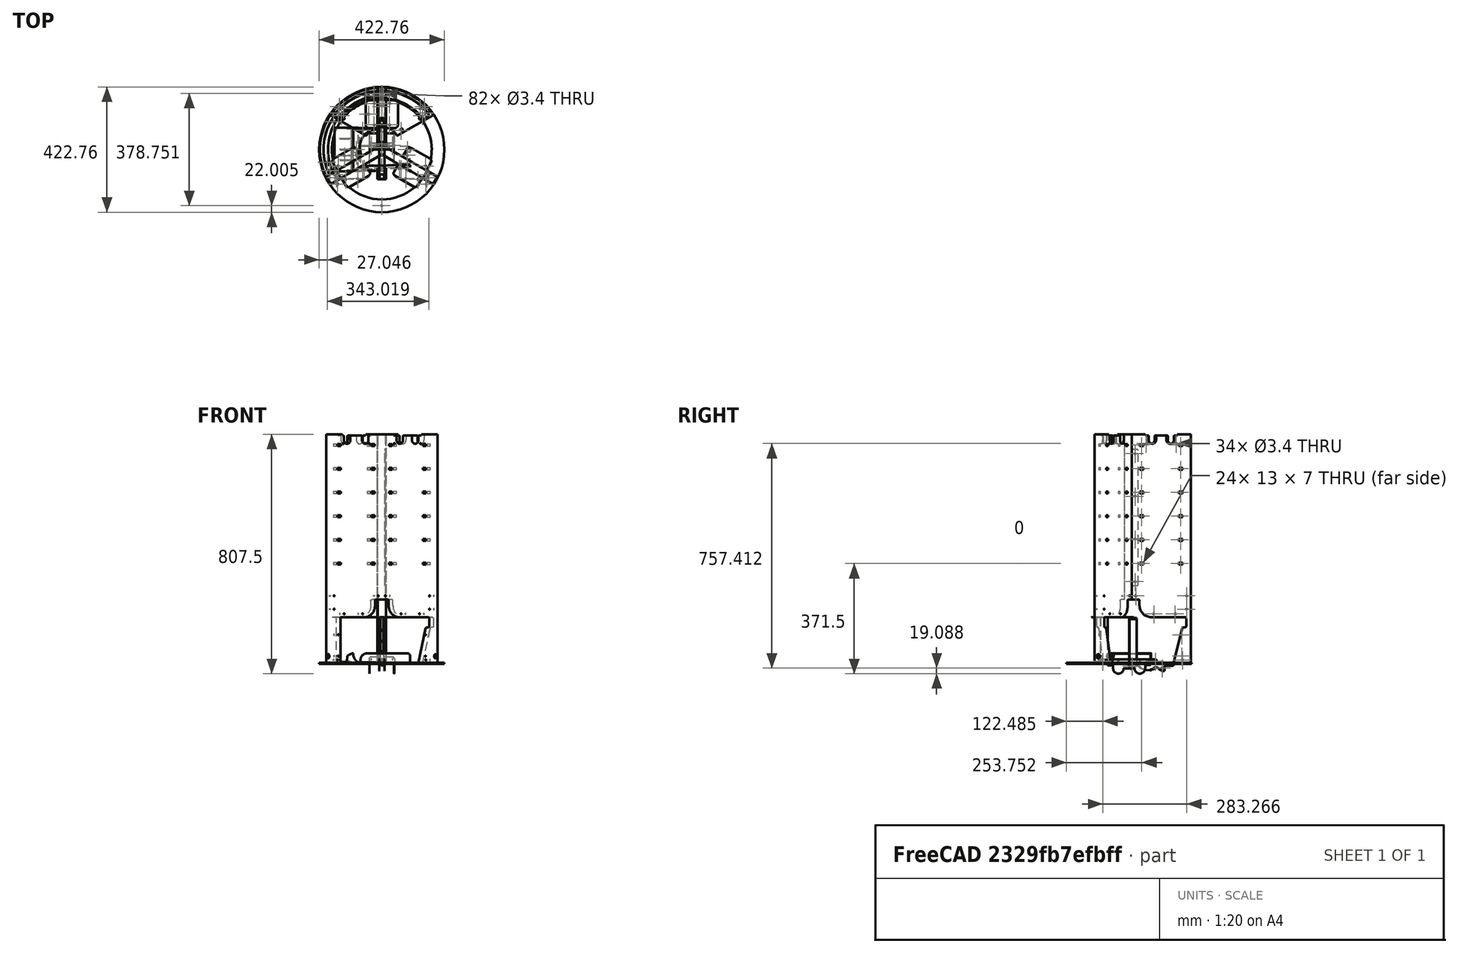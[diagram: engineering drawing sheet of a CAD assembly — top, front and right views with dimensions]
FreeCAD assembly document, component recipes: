
FREECAD ASSEMBLY — COMPONENT RECIPES ("composit_stand2_reserve")

This assembly document has 21 components, labeled P0..P20 below (a component is one placed body or linked part). 21 of them carry a construction recipe — the FreeCAD feature program that regenerates the part from scratch, quoted from this document or its linked companion documents; the rest are supplied as boundary geometry only. No exploded tour is included for this assembly.
NOTE — document 2 of 2 of this assembly tour. The two overview renders and the header above are repeated from document 1; the component sections below continue where the previous document stopped.
COMPONENT P18 — recipe-attached ("gutter_bottom_material_0.30ansi", modeled in this document).
Construction recipe (the document's own serialized feature program — sketch geometry with constraints, then the solid features built on it; lengths are millimeters unless a unit is written):

FEATURE [Sketcher::SketchObject] Sketch134
  FullyConstrained = true
  MapMode = 5
  Placement = pos=(0,0,0) rot=(1,0,0;1.5708rad)
  Support = -> [XZ_Plane044]
  sketch-geometry (5):
    g0: LineSegment StartX=-8.5 StartY=15 StartZ=0 EndX=-8.5 EndY=0 EndZ=0
    g1: LineSegment StartX=-8.5 StartY=0 StartZ=0 EndX=8.5 EndY=0 EndZ=0
    g2: LineSegment StartX=8.5 StartY=0 StartZ=0 EndX=8.5 EndY=15 EndZ=0
    g3: LineSegment StartX=8.5 StartY=15 StartZ=0 EndX=-8.5 EndY=15 EndZ=0
    g4: GeomPoint X=0 Y=7.5 Z=0
  constraints (13):
    c: Coincident(g0,g1)
    c: Coincident(g1,g2)
    c: Coincident(g2,g3)
    c: Coincident(g3,g0)
    c: Horizontal(g1)
    c: Horizontal(g3)
    c: Vertical(g0)
    c: Vertical(g2)
    c: Symmetric(g1,g0,g4)
    c: PointOnObject(g4,g-2)
    c: PointOnObject(g1,g-1)
    c: DistanceX(g1,g1) = 17  'width'
    c: DistanceY(g2) = 15  'height'
FEATURE [Sketcher::SketchObject] Sketch135
  FullyConstrained = true
  MapMode = 5
  Placement = pos=(0,0,0) rot=(1,0,0;1.5708rad)
  Support = -> [XZ_Plane044]
  sketch-geometry (1):
    g0: GeomPoint X=172 Y=45 Z=0
  constraints (3):
    c: DistanceX(g0) = 172
    c: DistanceY(g0) = 45
    c: Distance(g-1,g0) = 177.789  'length'
FEATURE [PartDesign::FeaturePython] BaseBend010  # WARN: FeaturePython — macro-defined, semantics opaque (R4)
  BendSide = 0
  BendSketch = -> Sketch134
  MidPlane = true
  Reverse = false
  length = 187.789
  radius = 0.1
  thickness = 0.3
FEATURE [Sketcher::SketchObject] Sketch136
  AttachmentOffset = pos=(0,8,0) rot=(0,0,1;0rad)
  FullyConstrained = true
  MapMode = 5
  Placement = pos=(-1.8e-15,1.8e-15,8) rot=(0.57735,0.57735,0.57735;2.0944rad)
  Support = -> [YZ_Plane044]
  sketch-geometry (2):
    g0: Circle CenterX=-88.8946 CenterY=0 CenterZ=0 NormalX=0 NormalY=0 NormalZ=1 AngleXU=0 Radius=1.7
    g1: Circle CenterX=88.8946 CenterY=0 CenterZ=0 NormalX=0 NormalY=0 NormalZ=1 AngleXU=0 Radius=1.7
  constraints (5):
    c: PointOnObject(g0,g-1)
    c: Symmetric(g0,g1,g-2)
    c: DistanceX(g0,g1) = 177.789
    c: Equal(g1,g0)
    c: Diameter(g1) = 3.4
FEATURE [Sketcher::SketchObject] Sketch137
  AttachmentOffset = pos=(93.8946,15,0) rot=(0,0,1;0rad)
  FullyConstrained = true
  MapMode = 5
  Placement = pos=(1.75e-14,93.8946,15) rot=(0.57735,0.57735,0.57735;2.0944rad)
  Support = -> [YZ_Plane044]
  sketch-geometry (3):
    g0: ArcOfCircle CenterX=-7 CenterY=-7 CenterZ=0 NormalX=0 NormalY=0 NormalZ=1 AngleXU=0 Radius=7 StartAngle=-3.2e-14 EndAngle=1.5708
    g1: LineSegment StartX=-7 StartY=0 StartZ=0 EndX=0 EndY=0 EndZ=0
    g2: LineSegment StartX=0 StartY=0 StartZ=0 EndX=0 EndY=-7 EndZ=0
  constraints (8):
    c: PointOnObject(g0,g-2)
    c: PointOnObject(g0,g-1)
    c: Coincident(g1,g2)
    c: Vertical(g2)
    c: Tangent(g2,g0) = 1.5708
    c: Tangent(g0,g1) = 1.5708
    c: DistanceY(g2,g2) = 7
    c: Horizontal(g1)
FEATURE [PartDesign::Pocket] Pocket092
  BaseFeature = -> BaseBend010
  Direction = (-1,2e-16,-3e-16)
  Length = 5
  Length2 = 5
  Midplane = true
  Profile = -> Sketch137
  ReferenceAxis = -> Sketch137 [N_Axis]
  Type = 1
FEATURE [PartDesign::Mirrored] Mirrored041
  BaseFeature = -> Pocket092
  MirrorPlane = -> XZ_Plane044
  Originals = -> [Pocket092]
FEATURE [Sketcher::SketchObject] Sketch138
  AttachmentOffset = pos=(0,-63.8946,0) rot=(0,0,1;0rad)
  FullyConstrained = false
  MapMode = 5
  Placement = pos=(0,-63.8946,0) rot=(0,0,1;0rad)
  Support = -> [XY_Plane045]
  sketch-geometry (5):
    g0: LineSegment StartX=-8.25 StartY=-159.942 StartZ=0 EndX=-8.25 EndY=0 EndZ=0
    g1: LineSegment StartX=-8.25 StartY=0 StartZ=0 EndX=8.25 EndY=0 EndZ=0
    g2: LineSegment StartX=8.25 StartY=0 StartZ=0 EndX=8.25 EndY=-159.942 EndZ=0
    g3: LineSegment StartX=8.25 StartY=-159.942 StartZ=0 EndX=-8.25 EndY=-159.942 EndZ=0
    g4: GeomPoint X=0 Y=-79.9711 Z=0
  constraints (12):
    c: Coincident(g0,g1)
    c: Coincident(g1,g2)
    c: Coincident(g2,g3)
    c: Coincident(g3,g0)
    c: Horizontal(g1)
    c: Horizontal(g3)
    c: Vertical(g0)
    c: Vertical(g2)
    c: Symmetric(g1,g0,g4)
    c: PointOnObject(g4,g-2)
    c: PointOnObject(g1,g-1)
    c: DistanceX(g1,g1) = 16.5
FEATURE [PartDesign::Pocket] Pocket093
  BaseFeature = -> Mirrored041
  Direction = (0,0,-1)
  Length = 5
  Length2 = 5
  Profile = -> Sketch138
  ReferenceAxis = -> Sketch138 [N_Axis]
  Type = 1
FEATURE [Sketcher::SketchObject] Sketch139
  AttachmentOffset = pos=(-93.8946,0,0) rot=(0,0,1;0rad)
  FullyConstrained = true
  MapMode = 5
  Placement = pos=(-2.08e-14,-93.8946,2.08e-14) rot=(0.57735,0.57735,0.57735;2.0944rad)
  Support = -> [YZ_Plane044]
  sketch-geometry (4):
    g0: ArcOfCircle CenterX=5 CenterY=5.1 CenterZ=0 NormalX=0 NormalY=0 NormalZ=1 AngleXU=0 Radius=5 StartAngle=3.14159 EndAngle=4.71239
    g1: LineSegment StartX=0 StartY=5.1 StartZ=0 EndX=0 EndY=-0.3 EndZ=0
    g2: LineSegment StartX=0 StartY=-0.3 StartZ=0 EndX=5 EndY=-0.3 EndZ=0
    g3: LineSegment StartX=5 StartY=-0.3 StartZ=0 EndX=5 EndY=0.1 EndZ=0
  constraints (12):
    c: PointOnObject(g0,g-2)
    c: PointOnObject(g1,g-2)
    c: Coincident(g2,g1)
    c: Horizontal(g2)
    c: Coincident(g3,g2)
    c: Coincident(g3,g0)
    c: Vertical(g3)
    c: Perpendicular(g0,g3)
    c: Tangent(g1,g0) = -1.5708
    c: DistanceY(g0) = 0.1
    c: Diameter(g0) = 10
    c: DistanceY(g1) = -0.3
FEATURE [PartDesign::Pocket] Pocket094
  BaseFeature = -> Pocket093
  Direction = (-1,2e-16,-3e-16)
  Length = 5
  Length2 = 5
  Midplane = true
  Profile = -> Sketch139
  ReferenceAxis = -> Sketch139 [N_Axis]
  Type = 1
FEATURE [Sketcher::SketchObject] Sketch140
  FullyConstrained = true
  MapMode = 5
  Placement = pos=(0,0,0) rot=(0.57735,0.57735,0.57735;2.0944rad)
  Support = -> [YZ_Plane044]
  sketch-geometry (4):
    g0: LineSegment StartX=-163.895 StartY=-10 StartZ=0 EndX=-63.8946 EndY=-10 EndZ=0
    g1: LineSegment StartX=-63.8946 StartY=-10 StartZ=0 EndX=-63.8946 EndY=0.11 EndZ=0
    g2: LineSegment StartX=-63.8946 StartY=0.11 StartZ=0 EndX=-163.895 EndY=0.11 EndZ=0
    g3: LineSegment StartX=-163.895 StartY=0.11 StartZ=0 EndX=-163.895 EndY=-10 EndZ=0
  constraints (12):
    c: Coincident(g0,g1)
    c: Coincident(g1,g2)
    c: Coincident(g2,g3)
    c: Coincident(g3,g0)
    c: Horizontal(g0)
    c: Horizontal(g2)
    c: Vertical(g1)
    c: Vertical(g3)
    c: DistanceY(g2) = 0.11
    c: DistanceX(g1) = -63.8946
    c: DistanceY(g0) = -10
    c: DistanceX(g2,g2) = 100
FEATURE [PartDesign::Pocket] Pocket095
  BaseFeature = -> Pocket094
  Direction = (-1,2e-16,-3e-16)
  Length = 5
  Length2 = 5
  Midplane = true
  Profile = -> Sketch140
  ReferenceAxis = -> Sketch140 [N_Axis]
  Type = 1
FEATURE [PartDesign::Pocket] Pocket091
  BaseFeature = -> Pocket095
  Direction = (-1,2e-16,-3e-16)
  Length = 5
  Length2 = 5
  Midplane = true
  Profile = -> Sketch136
  ReferenceAxis = -> Sketch136 [N_Axis]
  Type = 1
FEATURE [PartDesign::Body] gutter_bottom  label="gutter_bottom_material_0.30ansi"
  Group = -> [Sketch134,Sketch135,BaseBend010,Sketch136,Sketch137,Pocket092,Mirrored041,Sketch138,Pocket093,Sketch139,Pocket094,Sketch140,Pocket095,Pocket091]
  Origin = -> Origin044
  Tip = -> Pocket091
COMPONENT P19 — recipe-attached ("tech_mid_material_0.50ansi", modeled in this document).
Construction recipe (the document's own serialized feature program — sketch geometry with constraints, then the solid features built on it; lengths are millimeters unless a unit is written):

FEATURE [PartDesign::CoordinateSystem] LCS_0007
  AttacherType = Attacher::AttachEngine3D
  MapMode = 2
  Support = -> [X_Axis038]
FEATURE [Sketcher::SketchObject] Sketch122
  FullyConstrained = true
  MapMode = 5
  Placement = pos=(0,0,0) rot=(0.57735,0.57735,0.57735;2.0944rad)
  Support = -> [YZ_Plane038]
  sketch-geometry (4):
    g0: LineSegment StartX=0 StartY=0 StartZ=0 EndX=15 EndY=0 EndZ=0
    g1: LineSegment StartX=15 StartY=0 StartZ=0 EndX=15 EndY=151 EndZ=0
    g2: LineSegment StartX=15 StartY=151 StartZ=0 EndX=0 EndY=151 EndZ=0
    g3: LineSegment StartX=0 StartY=151 StartZ=0 EndX=0 EndY=0 EndZ=0
  constraints (11):
    c: Coincident(g0,g1)
    c: Coincident(g1,g2)
    c: Coincident(g2,g3)
    c: Coincident(g3,g0)
    c: Horizontal(g0)
    c: Horizontal(g2)
    c: Vertical(g1)
    c: Vertical(g3)
    c: Coincident(g0,g-1)
    c: DistanceY(g2) = 151  'height'
    c: DistanceX(g0,g0) = 15  'length'
FEATURE [PartDesign::FeaturePython] BaseBend009  # WARN: FeaturePython — macro-defined, semantics opaque (R4)
  BendSide = 1
  BendSketch = -> Sketch122
  MidPlane = true
  Reverse = false
  length = 10
  radius = 0.1
  thickness = 0.3
FEATURE [Sketcher::SketchObject] Sketch123
  FullyConstrained = true
  MapMode = 5
  Support = -> [XY_Plane039]
  sketch-geometry (3):
    g0: Circle CenterX=0 CenterY=7.5 CenterZ=0 NormalX=0 NormalY=0 NormalZ=1 AngleXU=0 Radius=1.7
    g1: LineSegment StartX=0 StartY=0 StartZ=0 EndX=0 EndY=7.5 EndZ=0
    g2: LineSegment StartX=0 StartY=7.5 StartZ=0 EndX=0 EndY=15 EndZ=0
  constraints (8):
    c: PointOnObject(g0,g-2)
    c: Diameter(g0) = 3.4
    c: Coincident(g1,g-1)
    c: Coincident(g1,g0)
    c: Coincident(g2,g0)
    c: PointOnObject(g2,g-2)
    c: Equal(g2,g1)
    c: DistanceY(g2) = 15
FEATURE [PartDesign::Pocket] Pocket076
  BaseFeature = -> BaseBend009
  Direction = (0,0,-1)
  Length = 5
  Length2 = 5
  Midplane = true
  Profile = -> Sketch123
  ReferenceAxis = -> Sketch123 [N_Axis]
  Type = 1
FEATURE [Sketcher::SketchObject] Sketch124
  FullyConstrained = true
  MapMode = 5
  Placement = pos=(0,0,0) rot=(1,0,0;1.5708rad)
  Support = -> [XZ_Plane038]
  sketch-geometry (2):
    g0: Circle CenterX=0 CenterY=75.5 CenterZ=0 NormalX=0 NormalY=0 NormalZ=1 AngleXU=0 Radius=1.7
    g1: GeomPoint X=0 Y=151 Z=0
  constraints (4):
    c: PointOnObject(g0,g-2)
    c: DistanceY(g1) = 151
    c: Symmetric(g1,g-1,g0)
    c: Diameter(g0) = 3.4
FEATURE [PartDesign::Pocket] Pocket077
  BaseFeature = -> Pocket076
  Direction = (0,1,2e-16)
  Length = 5
  Length2 = 5
  Midplane = true
  Profile = -> Sketch124
  ReferenceAxis = -> Sketch124 [N_Axis]
  Type = 1
FEATURE [PartDesign::Body] tech_mid  label="tech_mid_material_0.50ansi"
  Group = -> [LCS_0007,Sketch122,BaseBend009,Sketch123,Pocket076,Sketch124,Pocket077]
  Origin = -> Origin038
  Tip = -> Pocket077
COMPONENT P20 — recipe-attached ("tech_pillar_material_0.50ansi", modeled in this document).
Construction recipe (the document's own serialized feature program — sketch geometry with constraints, then the solid features built on it; lengths are millimeters unless a unit is written):

FEATURE [PartDesign::CoordinateSystem] LCS_0006
  AttacherType = Attacher::AttachEngine3D
  MapMode = 2
  Support = -> [X_Axis037]
FEATURE [Sketcher::SketchObject] Sketch116
  FullyConstrained = true
  MapMode = 5
  Placement = pos=(0,0,0) rot=(0.57735,0.57735,0.57735;2.0944rad)
  Support = -> [YZ_Plane037]
  sketch-geometry (4):
    g0: LineSegment StartX=0 StartY=0 StartZ=0 EndX=25 EndY=0 EndZ=0
    g1: LineSegment StartX=25 StartY=0 StartZ=0 EndX=25 EndY=154 EndZ=0
    g2: LineSegment StartX=25 StartY=154 StartZ=0 EndX=0 EndY=154 EndZ=0
    g3: LineSegment StartX=0 StartY=154 StartZ=0 EndX=0 EndY=0 EndZ=0
  constraints (11):
    c: Coincident(g0,g1)
    c: Coincident(g1,g2)
    c: Coincident(g2,g3)
    c: Coincident(g3,g0)
    c: Horizontal(g0)
    c: Horizontal(g2)
    c: Vertical(g1)
    c: Vertical(g3)
    c: Coincident(g0,g-1)
    c: Distance(g3) = 154  'height'
    c: DistanceX(g0) = 25  'length'
FEATURE [PartDesign::FeaturePython] BaseBend008  # WARN: FeaturePython — macro-defined, semantics opaque (R4)
  BendSide = 1
  BendSketch = -> Sketch116
  MidPlane = true
  Reverse = false
  length = 25
  radius = 0.01
  thickness = 0.3
FEATURE [PartDesign::FeaturePython] Bend015  # WARN: FeaturePython — macro-defined, semantics opaque (R4)
  AutoMiter = true
  BaseFeature = -> BaseBend008
  BendType = 0
  LengthList = [25]
  LengthSpec = 1
  ReliefFactor = 0.7
  UseReliefFactor = false
  angle = 90
  baseObject = -> BaseBend008 [Edge26]
  bendAList = [90]
  extend1 = 0
  extend2 = 0
  gap1 = 3
  gap2 = 3
  invert = false
  kfactor = 0.5
  length = 25
  maxExtendDist = 5
  minGap = 0.1
  minReliefGap = 1
  miterangle1 = 0
  miterangle2 = 0
  offset = 0
  radius = 0.01
  reliefType = 0
  reliefd = 0.1
  reliefw = 0.1
  sketchflip = false
  sketchinvert = false
  unfold = false
FEATURE [PartDesign::FeaturePython] Bend016  # WARN: FeaturePython — macro-defined, semantics opaque (R4)
  AutoMiter = true
  BaseFeature = -> Bend015
  BendType = 0
  LengthList = [25]
  LengthSpec = 0
  ReliefFactor = 0.7
  UseReliefFactor = false
  angle = 90
  baseObject = -> Bend015 [Edge3]
  bendAList = [90]
  extend1 = 0
  extend2 = 0
  gap1 = 3
  gap2 = 0
  invert = false
  kfactor = 0.5
  length = 25
  maxExtendDist = 5
  minGap = 0.1
  minReliefGap = 1
  miterangle1 = 0
  miterangle2 = 0
  offset = 0
  radius = 0.01
  reliefType = 0
  reliefd = 0.1
  reliefw = 0.1
  sketchflip = false
  sketchinvert = false
  unfold = false
FEATURE [PartDesign::FeaturePython] Bend017  # WARN: FeaturePython — macro-defined, semantics opaque (R4)
  AutoMiter = true
  BaseFeature = -> Bend016
  BendType = 0
  LengthList = [25]
  LengthSpec = 0
  ReliefFactor = 0.7
  UseReliefFactor = false
  angle = 90
  baseObject = -> Bend016 [Edge24]
  bendAList = [90]
  extend1 = 0
  extend2 = 0
  gap1 = 0
  gap2 = 3
  invert = false
  kfactor = 0.5
  length = 25
  maxExtendDist = 5
  minGap = 0.1
  minReliefGap = 1
  miterangle1 = 0
  miterangle2 = 0
  offset = 0
  radius = 0.01
  reliefType = 0
  reliefd = 0.1
  reliefw = 0.1
  sketchflip = false
  sketchinvert = false
  unfold = false
FEATURE [Sketcher::SketchObject] Sketch117
  FullyConstrained = true
  MapMode = 5
  Support = -> [XY_Plane038]
  sketch-geometry (5):
    g0: Circle CenterX=0 CenterY=6 CenterZ=0 NormalX=0 NormalY=0 NormalZ=1 AngleXU=0 Radius=1.7
    g1: Circle CenterX=0 CenterY=19 CenterZ=0 NormalX=0 NormalY=0 NormalZ=1 AngleXU=0 Radius=1.7
    g2: LineSegment StartX=0 StartY=0 StartZ=0 EndX=0 EndY=6 EndZ=0
    g3: LineSegment StartX=0 StartY=6 StartZ=0 EndX=0 EndY=19 EndZ=0
    g4: LineSegment StartX=0 StartY=19 StartZ=0 EndX=0 EndY=25 EndZ=0
  constraints (13):
    c: PointOnObject(g0,g-2)
    c: PointOnObject(g1,g-2)
    c: Coincident(g2,g-1)
    c: Coincident(g2,g0)
    c: Coincident(g3,g0)
    c: Coincident(g3,g1)
    c: Coincident(g4,g1)
    c: PointOnObject(g4,g-2)
    c: DistanceY(g4) = 25
    c: Equal(g2,g4)
    c: Distance(g2) = 6
    c: Equal(g0,g1)
    c: Diameter(g0) = 3.4
FEATURE [PartDesign::Pocket] Pocket071
  BaseFeature = -> Bend017
  Direction = (0,0,-1)
  Length = 5
  Length2 = 5
  Midplane = true
  Profile = -> Sketch117
  ReferenceAxis = -> Sketch117 [N_Axis]
  Type = 1
FEATURE [Sketcher::SketchObject] Sketch118
  FullyConstrained = true
  MapMode = 5
  Placement = pos=(0,0,0) rot=(0.57735,0.57735,0.57735;2.0944rad)
  Support = -> [YZ_Plane037]
  sketch-geometry (4):
    g0: LineSegment StartX=60 StartY=130 StartZ=0 EndX=160 EndY=130 EndZ=0
    g1: LineSegment StartX=160 StartY=130 StartZ=0 EndX=160 EndY=180 EndZ=0
    g2: LineSegment StartX=160 StartY=180 StartZ=0 EndX=60 EndY=180 EndZ=0
    g3: LineSegment StartX=60 StartY=180 StartZ=0 EndX=60 EndY=130 EndZ=0
  constraints (12):
    c: Coincident(g0,g1)
    c: Coincident(g1,g2)
    c: Coincident(g2,g3)
    c: Coincident(g3,g0)
    c: Horizontal(g0)
    c: Horizontal(g2)
    c: Vertical(g1)
    c: Vertical(g3)
    c: DistanceY(g3,g3) = 50  'height'
    c: DistanceX(g0,g0) = 100  'length'
    c: DistanceX(g0) = 60
    c: DistanceY(g0) = 130
FEATURE [Sketcher::SketchObject] Sketch126
  FullyConstrained = true
  MapMode = 5
  Support = -> [XY_Plane038]
  sketch-geometry (3):
    g0: LineSegment StartX=12.5 StartY=25 StartZ=0 EndX=12.5 EndY=17.5 EndZ=0
    g1: LineSegment StartX=12.5 StartY=25 StartZ=0 EndX=5 EndY=25 EndZ=0
    g2: ArcOfCircle CenterX=5 CenterY=17.5 CenterZ=0 NormalX=0 NormalY=0 NormalZ=1 AngleXU=0 Radius=7.5 StartAngle=0 EndAngle=1.5708
  constraints (8):
    c: Vertical(g0)
    c: DistanceX(g0) = 12.5
    c: DistanceY(g0) = 25
    c: Coincident(g1,g0)
    c: Horizontal(g1)
    c: Tangent(g2,g0) = 1.5708
    c: Tangent(g2,g1) = -1.5708
    c: Diameter(g2) = 15
FEATURE [PartDesign::Pocket] Pocket080
  BaseFeature = -> Pocket071
  Direction = (0,0,-1)
  Length = 5
  Length2 = 5
  Midplane = true
  Profile = -> Sketch126
  ReferenceAxis = -> Sketch126 [N_Axis]
  Type = 1
FEATURE [Sketcher::SketchObject] Sketch127
  FullyConstrained = true
  MapMode = 5
  Placement = pos=(0,0,0) rot=(0.57735,0.57735,0.57735;2.0944rad)
  Support = -> [YZ_Plane037]
  sketch-geometry (4):
    g0: LineSegment StartX=71.78 StartY=114.36 StartZ=0 EndX=143.27 EndY=114.36 EndZ=0
    g1: LineSegment StartX=143.27 StartY=114.36 StartZ=0 EndX=143.27 EndY=159.55 EndZ=0
    g2: LineSegment StartX=143.27 StartY=159.55 StartZ=0 EndX=71.78 EndY=159.55 EndZ=0
    g3: LineSegment StartX=71.78 StartY=159.55 StartZ=0 EndX=71.78 EndY=114.36 EndZ=0
  constraints (12):
    c: Coincident(g0,g1)
    c: Coincident(g1,g2)
    c: Coincident(g2,g3)
    c: Coincident(g3,g0)
    c: Horizontal(g0)
    c: Horizontal(g2)
    c: Vertical(g1)
    c: Vertical(g3)
    c: DistanceX(g0) = 71.78  'offset_x'
    c: DistanceY(g0) = 114.36  'offset_y'
    c: DistanceY(g3,g3) = 45.19  'height'
    c: DistanceX(g0,g0) = 71.49  'width'
FEATURE [Sketcher::SketchObject] Sketch133
  FullyConstrained = true
  MapMode = 5
  Placement = pos=(0,0,0) rot=(1,0,0;1.5708rad)
  Support = -> [XZ_Plane037]
  sketch-geometry (4):
    g0: Circle CenterX=0 CenterY=41 CenterZ=0 NormalX=0 NormalY=0 NormalZ=1 AngleXU=0 Radius=1.7
    g1: Circle CenterX=0 CenterY=113 CenterZ=0 NormalX=0 NormalY=0 NormalZ=1 AngleXU=0 Radius=1.7
    g2: GeomPoint X=0 Y=77 Z=0
    g3: GeomPoint X=0 Y=154 Z=0
  constraints (8):
    c: PointOnObject(g0,g-2)
    c: PointOnObject(g1,g-2)
    c: DistanceY(g3) = 154
    c: Symmetric(g3,g-1,g2)
    c: Symmetric(g0,g1,g2)
    c: DistanceY(g0,g1) = 72
    c: Equal(g0,g1)
    c: Diameter(g0) = 3.4
FEATURE [PartDesign::Pocket] Pocket090
  BaseFeature = -> Pocket080
  Direction = (0,1,2e-16)
  Length = 5
  Length2 = 5
  Midplane = true
  Profile = -> Sketch133
  ReferenceAxis = -> Sketch133 [N_Axis]
  Type = 1
FEATURE [PartDesign::Body] tech_pillar  label="tech_pillar_material_0.50ansi"
  Group = -> [LCS_0006,Sketch116,BaseBend008,Bend015,Bend016,Bend017,Sketch117,Pocket071,Sketch118,Sketch126,Pocket080,Sketch127,Sketch133,Pocket090]
  Origin = -> Origin037
  Tip = -> Pocket090
PROVENANCE & LICENSES
A FreeCAD (.FCStd) document from a public repository crawl; recipes are the document's own serialized feature recipes (and, for linked parts, companion documents' recipes).
License: as declared in the source repository (recorded in the dataset sidecar).
